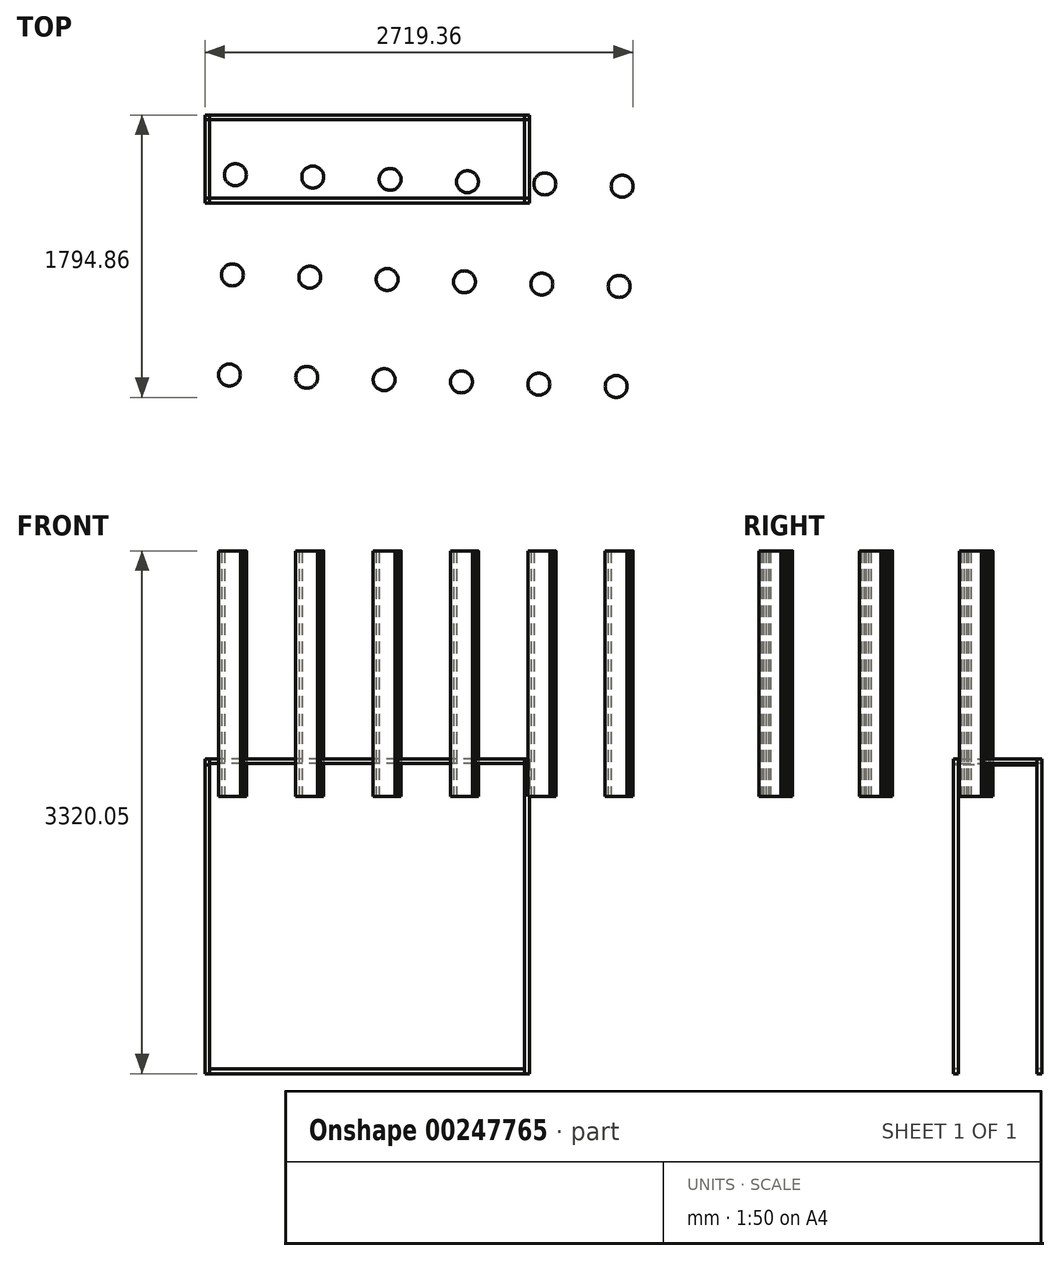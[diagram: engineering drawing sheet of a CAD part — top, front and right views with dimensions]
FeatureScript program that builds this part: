
annotation { "Feature Type Name" : "Feature", "Feature Type Description" : "" }
export const myFeature = defineFeature(function(context is Context, id is Id, definition is map)
    precondition{}
    {
        {
            var Q0;
            Q0=qCreatedBy(makeId("Top.planeOp"),FACE);
            var sketch = newSketch(context, id + "F0", { "sketchPlane" : qUnion([Q0])});
            skLineSegment(sketch, "E0.bottom", {"start": v(-1000, 280) * mm, "end": v(-1030, 280) * mm});
            skLineSegment(sketch, "E0.top", {"start": v(-1000, 250) * mm, "end": v(-1030, 250) * mm});
            skLineSegment(sketch, "E0.left", {"start": v(-1000, 280) * mm, "end": v(-1000, 250) * mm});
            skLineSegment(sketch, "E0.right", {"start": v(-1030, 280) * mm, "end": v(-1030, 250) * mm});
            skPoint(sketch, "E0.middle", {"position": v(-1015, 265) * mm});
            skLineSegment(sketch, "E1.MirrorCS", {"start": v(1030, 280) * mm, "end": v(1030, 250) * mm});
            skLineSegment(sketch, "E2.MirrorCS", {"start": v(1000, 280) * mm, "end": v(1030, 280) * mm});
            skLineSegment(sketch, "E3.MirrorCS", {"start": v(1000, 280) * mm, "end": v(1000, 250) * mm});
            skLineSegment(sketch, "E4.MirrorCS", {"start": v(1000, 250) * mm, "end": v(1030, 250) * mm});
            skPoint(sketch, "E5.MirrorP", {"position": v(-1015, -265) * mm});
            skLineSegment(sketch, "E6.MirrorCS", {"start": v(-1000, -280) * mm, "end": v(-1030, -280) * mm});
            skLineSegment(sketch, "E7.MirrorCS", {"start": v(-1000, -280) * mm, "end": v(-1000, -250) * mm});
            skLineSegment(sketch, "E8.MirrorCS", {"start": v(-1000, -250) * mm, "end": v(-1030, -250) * mm});
            skLineSegment(sketch, "E9.MirrorCS", {"start": v(-1030, -280) * mm, "end": v(-1030, -250) * mm});
            skLineSegment(sketch, "E10.MirrorCS", {"start": v(1000, -280) * mm, "end": v(1000, -250) * mm});
            skLineSegment(sketch, "E11.MirrorCS", {"start": v(1000, -280) * mm, "end": v(1030, -280) * mm});
            skLineSegment(sketch, "E12.MirrorCS", {"start": v(1030, -280) * mm, "end": v(1030, -250) * mm});
            skLineSegment(sketch, "E13.MirrorCS", {"start": v(1000, -250) * mm, "end": v(1030, -250) * mm});
            skSolve(sketch);
        }
        {
            var Q0;
            Q0 = qSketchRegion(id + "F0", true);
            extrude(context, id + "F1", {"entities" : qUnion([Q0]), "depth" : 2000 * mm});
        }
        {
            var Q0;
            Q0=makeQuery(id+"F1.opExtrude","SWEPT_FACE",FACE,{"disambiguationData":[OSD([sQuery(id+"F0.wireOp",EDGE,"E0.left")])]});
            var sketch = newSketch(context, id + "F2", { "sketchPlane" : qUnion([Q0])});
            skLineSegment(sketch, "E14.bottom", {"start": v(280, 30) * mm, "end": v(250, 30) * mm});
            skLineSegment(sketch, "E14.top", {"start": v(280, 0) * mm, "end": v(250, 0) * mm});
            skLineSegment(sketch, "E14.left", {"start": v(280, 30) * mm, "end": v(280, 0) * mm});
            skLineSegment(sketch, "E14.right", {"start": v(250, 30) * mm, "end": v(250, 0) * mm});
            skPoint(sketch, "E14.middle", {"position": v(265, 15) * mm});
            skLineSegment(sketch, "E15.MirrorCS", {"start": v(-280, 30) * mm, "end": v(-250, 30) * mm});
            skLineSegment(sketch, "E16.MirrorCS", {"start": v(-250, 30) * mm, "end": v(-250, 0) * mm});
            skLineSegment(sketch, "E17.MirrorCS", {"start": v(-280, 0) * mm, "end": v(-250, 0) * mm});
            skLineSegment(sketch, "E18.MirrorCS", {"start": v(-280, 30) * mm, "end": v(-280, 0) * mm});
            skSolve(sketch);
        }
        {
            var Q0;
            Q0 = qSketchRegion(id + "F2", true);
            extrude(context, id + "F3", {"entities" : qUnion([Q0]), "endBound" : BoundingType.UP_TO_NEXT, "depth" : 25 * mm});
        }
        {
            var Q0;
            Q0=makeQuery(id+"F1.opExtrude","SWEPT_FACE",FACE,{"disambiguationData":[OSD([sQuery(id+"F0.wireOp",EDGE,"E7.MirrorCS")])]});
            var sketch = newSketch(context, id + "F4", { "sketchPlane" : qUnion([Q0])});
            skLineSegment(sketch, "E19.bottom", {"start": v(-250, 2000) * mm, "end": v(-280, 2000) * mm});
            skLineSegment(sketch, "E19.top", {"start": v(-250, 1970) * mm, "end": v(-280, 1970) * mm});
            skLineSegment(sketch, "E19.left", {"start": v(-250, 2000) * mm, "end": v(-250, 1970) * mm});
            skLineSegment(sketch, "E19.right", {"start": v(-280, 2000) * mm, "end": v(-280, 1970) * mm});
            skLineSegment(sketch, "E20.bottom", {"start": v(280, 2000) * mm, "end": v(250, 2000) * mm});
            skLineSegment(sketch, "E20.top", {"start": v(280, 1970) * mm, "end": v(250, 1970) * mm});
            skLineSegment(sketch, "E20.left", {"start": v(280, 2000) * mm, "end": v(280, 1970) * mm});
            skLineSegment(sketch, "E20.right", {"start": v(250, 2000) * mm, "end": v(250, 1970) * mm});
            skSolve(sketch);
        }
        {
            var Q0;
            Q0 = qSketchRegion(id + "F4", true);
            extrude(context, id + "F5", {"entities" : qUnion([Q0]), "endBound" : BoundingType.UP_TO_NEXT, "depth" : 25 * mm});
        }
        {
            var Q0;
            Q0=makeQuery(id+"F1.opExtrude","SWEPT_FACE",FACE,{"disambiguationData":[OSD([sQuery(id+"F0.wireOp",EDGE,"E6.MirrorCS")])]});
            var sketch = newSketch(context, id + "F6", { "sketchPlane" : qUnion([Q0])});
            skLineSegment(sketch, "E21.bottom", {"start": v(-1000, 2000) * mm, "end": v(-1030, 2000) * mm});
            skLineSegment(sketch, "E21.top", {"start": v(-1000, 1962.48) * mm, "end": v(-1030, 1962.48) * mm});
            skLineSegment(sketch, "E21.left", {"start": v(-1000, 2000) * mm, "end": v(-1000, 1962.48) * mm});
            skLineSegment(sketch, "E21.right", {"start": v(-1030, 2000) * mm, "end": v(-1030, 1962.48) * mm});
            skSolve(sketch);
        }
        {
            var Q0;
            Q0=makeQuery(id+"F6.imprint","IMPRINT",FACE,{"disambiguationData":[TD([[makeQuery(id+"F6.imprint","IMPRINT",EDGE,{"derivedFrom":sQuery(id+"F6.wireOp",EDGE,"E21.bottom")}),1.0]])]});
            var Q1;
            Q1=makeQuery(id+"F1.opExtrude","SWEPT_FACE",FACE,{"disambiguationData":[OSD([sQuery(id+"F0.wireOp",EDGE,"E0.top")])]});
            extrude(context, id + "F7", {"entities" : qUnion([Q0]), "endBound" : BoundingType.UP_TO_SURFACE, "oppositeDirection" : true, "endBoundEntityFace" : qUnion([Q1]), "depth" : 97.06 * mm});
        }
        {
            var Q0;
            Q0=makeQuery(id+"F1.opExtrude","SWEPT_FACE",FACE,{"disambiguationData":[OSD([sQuery(id+"F0.wireOp",EDGE,"E4.MirrorCS")])]});
            var sketch = newSketch(context, id + "F8", { "sketchPlane" : qUnion([Q0])});
            skLineSegment(sketch, "E22.bottom", {"start": v(1030, 2000) * mm, "end": v(1000, 2000) * mm});
            skLineSegment(sketch, "E22.top", {"start": v(1030, 1970) * mm, "end": v(1000, 1970) * mm});
            skLineSegment(sketch, "E22.left", {"start": v(1030, 2000) * mm, "end": v(1030, 1970) * mm});
            skLineSegment(sketch, "E22.right", {"start": v(1000, 2000) * mm, "end": v(1000, 1970) * mm});
            skSolve(sketch);
        }
        {
            var Q0;
            Q0 = qSketchRegion(id + "F8", true);
            extrude(context, id + "F9", {"entities" : qUnion([Q0]), "depth" : 500 * mm});
        }
        {
            var Q0;
            Q0=makeQuery(id+"F1.opExtrude","SWEPT_FACE",FACE,{"disambiguationData":[OSD([sQuery(id+"F0.wireOp",EDGE,"E6.MirrorCS")])]});
            var sketch = newSketch(context, id + "F10", { "sketchPlane" : qUnion([Q0])});
            skLineSegment(sketch, "E23.bottom", {"start": v(-1030, 1760.2) * mm, "end": v(998.26, 1760.2) * mm});
            skLineSegment(sketch, "E23.top", {"start": v(-1030, 1721.32) * mm, "end": v(998.26, 1721.32) * mm});
            skLineSegment(sketch, "E23.left", {"start": v(-1030, 1760.2) * mm, "end": v(-1030, 1721.32) * mm});
            skLineSegment(sketch, "E23.right", {"start": v(998.26, 1760.2) * mm, "end": v(998.26, 1721.32) * mm});
            skSolve(sketch);
        }
        {
            var Q0;
            Q0=sQuery(id+"F10.wireOp",EDGE,"E23.top");
            var Q1;
            Q1 = qBodyType(qCreatedBy(id + "F10" ,EDGE), BodyType.WIRE);
            extrude(context, id + "F11", {"bodyType" : ToolBodyType.SURFACE, "surfaceEntities" : qUnion([Q0, Q1]), "oppositeDirection" : true, "depth" : 450 * mm});
        }
        {
            var Q0;
            Q0=makeQuery(id+"F11.opExtrude","SWEPT_FACE",FACE,{"disambiguationData":[OSD([sQuery(id+"F10.wireOp",EDGE,"E23.bottom")])]});
            var sketch = newSketch(context, id + "F12", { "sketchPlane" : qUnion([Q0])});
            skCircle(sketch, "E24", {"center": v(-836.72, 100.23) * mm, "radius": 69.62 * mm});
            skCircle(sketch, "E25.0.1.0", {"center": v(-855.72, 736.19) * mm, "radius": 69.62 * mm});
            skCircle(sketch, "E25.1.0.0", {"center": v(-345.43, 114.84) * mm, "radius": 69.62 * mm});
            skCircle(sketch, "E25.1.1.0", {"center": v(-364.43, 750.8) * mm, "radius": 69.62 * mm});
            skCircle(sketch, "E25.2.0.0", {"center": v(145.87, 129.46) * mm, "radius": 69.62 * mm});
            skCircle(sketch, "E25.2.1.0", {"center": v(126.86, 765.42) * mm, "radius": 69.62 * mm});
            skLineSegment(sketch, "E25.direction1", {"start": v(-836.72, 100.23) * mm, "end": v(-345.43, 114.84) * mm, "construction": true});
            skLineSegment(sketch, "E25.direction2", {"start": v(-836.72, 100.23) * mm, "end": v(-855.72, 736.19) * mm, "construction": true});
            skCircle(sketch, "E26.0.0.2", {"center": v(-874.72, 1372.15) * mm, "radius": 69.62 * mm});
            skCircle(sketch, "E26.0.1.2", {"center": v(-383.43, 1386.77) * mm, "radius": 69.62 * mm});
            skCircle(sketch, "E26.0.2.2", {"center": v(107.86, 1401.38) * mm, "radius": 69.62 * mm});
            skCircle(sketch, "E27.0.3.0", {"center": v(637.16, 144.07) * mm, "radius": 69.62 * mm});
            skCircle(sketch, "E27.0.3.1", {"center": v(618.15, 780.04) * mm, "radius": 69.62 * mm});
            skCircle(sketch, "E27.0.3.2", {"center": v(599.15, 1416) * mm, "radius": 69.62 * mm});
            skCircle(sketch, "E27.0.4.0", {"center": v(1128.45, 158.7) * mm, "radius": 69.62 * mm});
            skCircle(sketch, "E27.0.4.1", {"center": v(1109.45, 794.65) * mm, "radius": 69.62 * mm});
            skCircle(sketch, "E27.0.4.2", {"center": v(1090.44, 1430.62) * mm, "radius": 69.62 * mm});
            skCircle(sketch, "E28.0.5.0", {"center": v(1619.74, 173.3) * mm, "radius": 69.62 * mm});
            skCircle(sketch, "E28.0.5.1", {"center": v(1600.74, 809.27) * mm, "radius": 69.62 * mm});
            skCircle(sketch, "E28.0.5.2", {"center": v(1581.74, 1445.23) * mm, "radius": 69.62 * mm});
            skSolve(sketch);
        }
        {
            var Q0;
            Q0 = qSketchRegion(id + "F12", true);
            extrude(context, id + "F13", {"entities" : qUnion([Q0]), "oppositeDirection" : true, "depth" : 1559.85 * mm});
        }
    });
